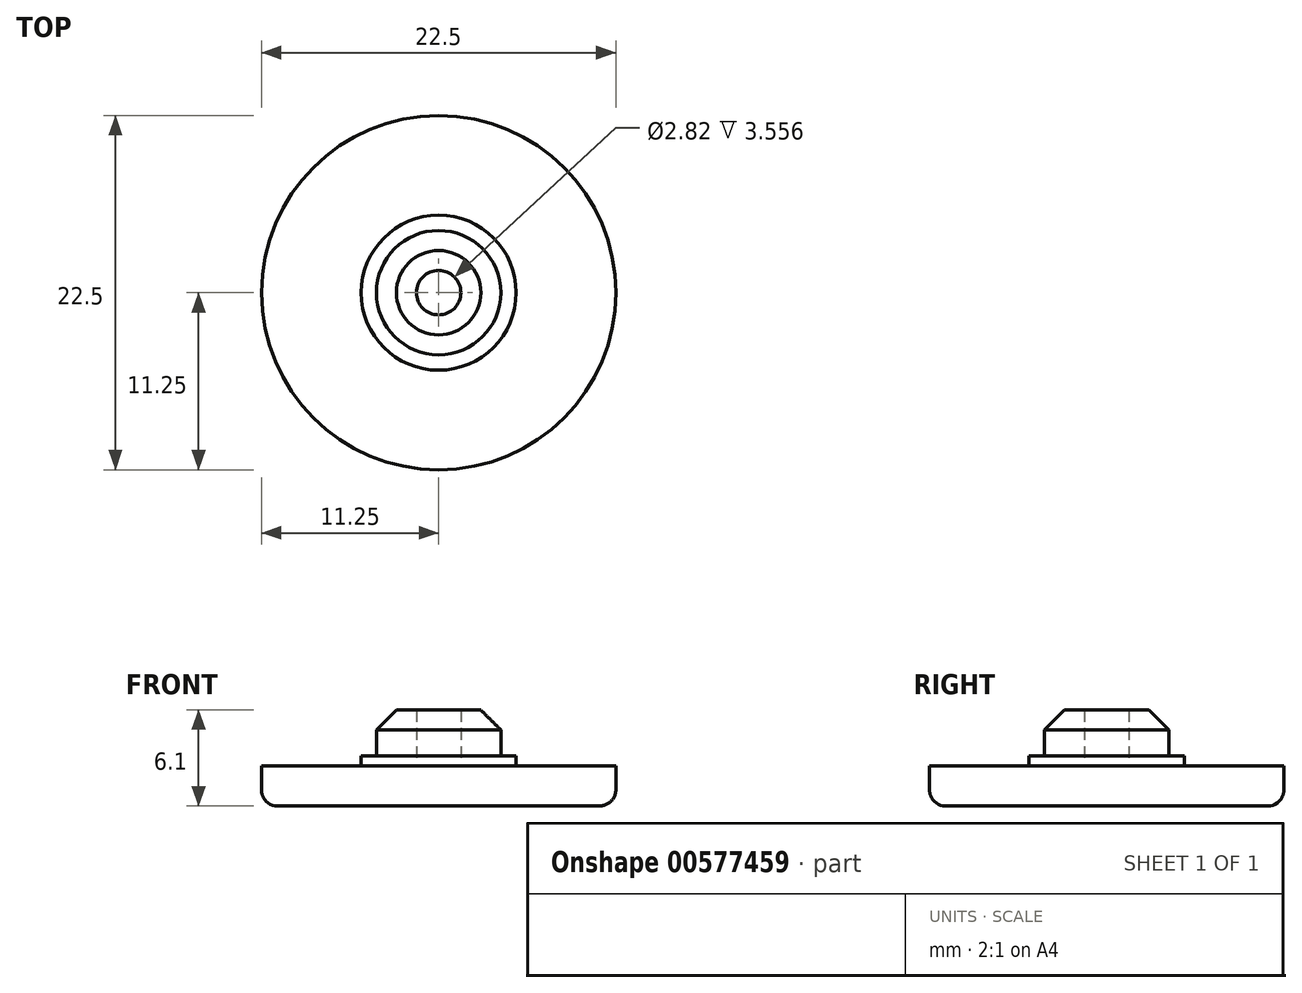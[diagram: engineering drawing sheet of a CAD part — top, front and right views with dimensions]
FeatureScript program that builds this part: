
annotation { "Feature Type Name" : "Feature", "Feature Type Description" : "" }
export const myFeature = defineFeature(function(context is Context, id is Id, definition is map)
    precondition{}
    {
        {
            var Q0;
            Q0=qCreatedBy(makeId("Top.planeOp"),FACE);
            var sketch = newSketch(context, id + "F0", { "sketchPlane" : qUnion([Q0])});
            skCircle(sketch, "E0", {"center": v(0, 0) * mm, "radius": 3.95 * mm});
            skCircle(sketch, "E1", {"center": v(0, 0) * mm, "radius": 11.25 * mm});
            skSolve(sketch);
        }
        {
            var Q0;
            Q0=makeQuery(id+"F0.imprint","IMPRINT",FACE,{"disambiguationData":[TD([[makeQuery(id+"F0.imprint","IMPRINT",EDGE,{"derivedFrom":sQuery(id+"F0.wireOp",EDGE,"E0")}),1.0]])]});
            extrude(context, id + "F1", {"entities" : qUnion([Q0]), "depth" : 3.56 * mm, "offsetDistance" : 25.4 * mm});
        }
        {
            var Q0;
            Q0=makeQuery(id+"F0.imprint","IMPRINT",FACE,{"disambiguationData":[TD([[makeQuery(id+"F0.imprint","IMPRINT",EDGE,{"derivedFrom":sQuery(id+"F0.wireOp",EDGE,"E0")}),-1.0]])]});
            var Q1;
            Q1=makeQuery(id+"F0.imprint","IMPRINT",FACE,{"disambiguationData":[TD([[makeQuery(id+"F0.imprint","IMPRINT",EDGE,{"derivedFrom":sQuery(id+"F0.wireOp",EDGE,"E0")}),1.0]])]});
            extrude(context, id + "F2", {"entities" : qUnion([Q0, Q1]), "operationType" : NewBodyOperationType.ADD, "oppositeDirection" : true, "depth" : 2.54 * mm, "offsetDistance" : 25.4 * mm});
        }
        {
            var Q0;
            Q0=makeQuery(id+"F2.opExtrude","CAP_EDGE",EDGE,{"disambiguationData":[OSD([sQuery(id+"F0.wireOp",EDGE,"E1")])],"isStart":false});
            fillet(context, id + "F3", {"entities" : qUnion([Q0]), "radius" : 1.02 * mm, "tangentPropagation" : true, "allowEdgeOverflow" : false});
        }
        {
            var Q0;
            Q0=makeQuery(id+"F0.imprint","IMPRINT",FACE,{"disambiguationData":[TD([[makeQuery(id+"F0.imprint","IMPRINT",EDGE,{"derivedFrom":sQuery(id+"F0.wireOp",EDGE,"E0")}),-1.0]])]});
            var sketch = newSketch(context, id + "F4", { "sketchPlane" : qUnion([Q0])});
            skCircle(sketch, "E2", {"center": v(0, 0) * mm, "radius": 4.92 * mm});
            skSolve(sketch);
        }
        {
            var Q0;
            Q0=makeQuery(id+"F4.imprint","IMPRINT",FACE,{"disambiguationData":[TD([[makeQuery(id+"F4.imprint","IMPRINT",EDGE,{"derivedFrom":sQuery(id+"F4.wireOp",EDGE,"E2")}),1.0]])]});
            extrude(context, id + "F5", {"entities" : qUnion([Q0]), "operationType" : NewBodyOperationType.ADD, "endBound" : BoundingType.SYMMETRIC, "depth" : 1.27 * mm, "offsetDistance" : 25.4 * mm});
        }
        {
            var Q0;
            Q0=makeQuery(id+"F1.opExtrude","CAP_FACE",FACE,{"disambiguationData":[OSD([sQuery(id+"F0.wireOp",EDGE,"E0")])],"isStart":false});
            shell(context, id + "F6", {"entities" : qUnion([Q0]), "thickness" : 2.54 * mm});
        }
        {
            var Q0;
            Q0=makeQuery(id+"F1.opExtrude","CAP_EDGE",EDGE,{"disambiguationData":[OSD([sQuery(id+"F0.wireOp",EDGE,"E0")])],"isStart":false});
            chamfer(context, id + "F7", {"entities" : qUnion([Q0]), "width" : 1.27 * mm, "tangentPropagation" : true});
        }
    });
